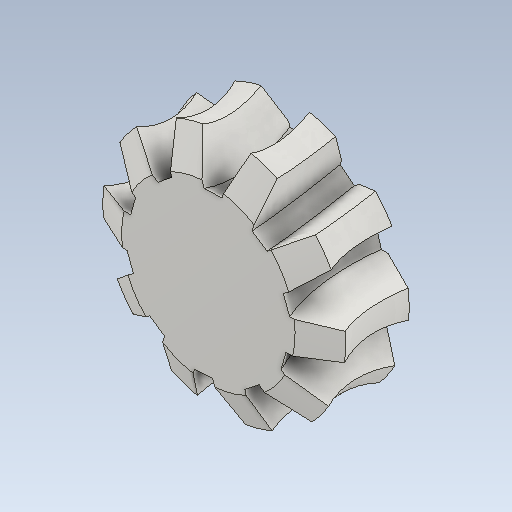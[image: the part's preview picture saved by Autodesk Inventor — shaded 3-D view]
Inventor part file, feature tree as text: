
AUTODESK INVENTOR PART (.ipt)
format: ipt  version: 2021 (Build 250183000, 183)  size: 311,296 bytes
history: native  units: mm (DEFAULTED — no unit token found)
features: other x8, plane x3, pattern_circular x1, sketch x1
ambient origin geometry x5: Origin, X Axis, Y Axis, Z Axis, Center Point
bodies: Solid1 (feature_tree)
feature tree (13):
  other  "Tooth Plane"
  other  "Base Body Sketch"
  other  "Base Body"
  other  "Base Body2"
  plane  "Work Plane13"
  other  "Tooth"
  pattern_circular  "Tooth Pattern"  [2 undecoded]
  plane  "Work Plane14"
  plane  "Work Plane15"
  other  "Tooth Sketch"
  sketch  "Sketch8"  dims[d35=90.0deg d37=-0.996687mm d38=40.0168mm d39=3.490659mm d40=14.8mm d41=20.0mm d42=3.769911mm d43=90.0deg d44=100.0mm d46=360.0deg d50=4.297754mm d68=40.0168mm d69=0.0mm d73=0.0mm d75=3.141593mm d77=40.0mm d78=20.0mm d79=0.0mm d80=0.0mm d81=0.0mm d82=0.0mm d83=3.141593mm d84=0.0mm d85=180.0deg d86=40.0168mm d87=52.0336mm d89=32.0mm d90=90.0deg d92=20.0mm d93=40.0168mm]
  other  "Srf1"
  other  "Pitch Diameter"
note: 2 required parameter values undecoded (feature->parameter linkage not recoverable at this tier; creation-order binding heuristic only, values carry confidence <= 0.55)
